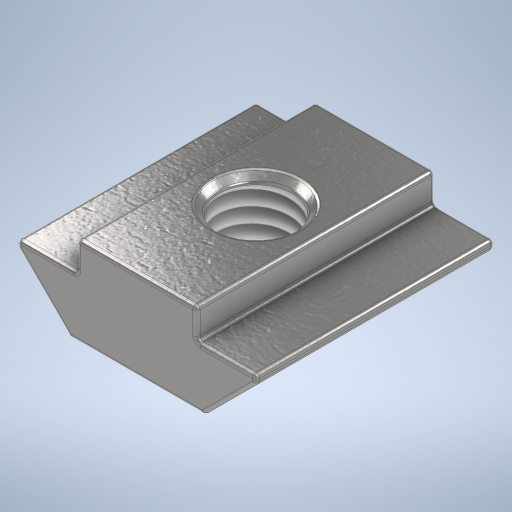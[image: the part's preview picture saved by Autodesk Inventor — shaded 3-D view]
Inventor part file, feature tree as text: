
AUTODESK INVENTOR PART (.ipt)
format: ipt  version: 2024 (Build 280153000, 153)  size: 400,384 bytes
history: native  units: mm
features: chamfer x2, sketch x2, extrude x1, hole x1, fillet x1
ambient origin geometry x8: Origin, YZ Plane, XZ Plane, XY Plane, X Axis, Y Axis, Z Axis, Center Point
bodies: Solid1 (feature_tree)
feature tree (7):
  extrude  "Extrusion1"  Depth=4.0mm
  chamfer  "Chamfer1"  Distance=8.0mm
  hole  "Hole1"  [1 undecoded]
  chamfer  "Chamfer2"  Distance=2.0mm Angle=45.0deg
  fillet  "Fillet1"  Radius=0.5mm
  sketch  "Sketch1"  dims[d0=2.0mm d1=4.0mm]
  sketch  "Sketch2"  dims[d2=16.0mm d3=8.0mm d4=16.0mm d5=0.0mm d6=3.5mm d7=2.0mm d8=45.0deg d9=4.917mm d10=12.0mm d11=4.0mm d12=2.0mm d13=90.0deg d14=8.0mm d15=20.594885mm d16=0.5mm d17=2.0mm d18=45.0deg d19=0.25mm]
note: 1 required parameter value undecoded (feature->parameter linkage not recoverable at this tier; creation-order binding heuristic only, values carry confidence <= 0.55)
